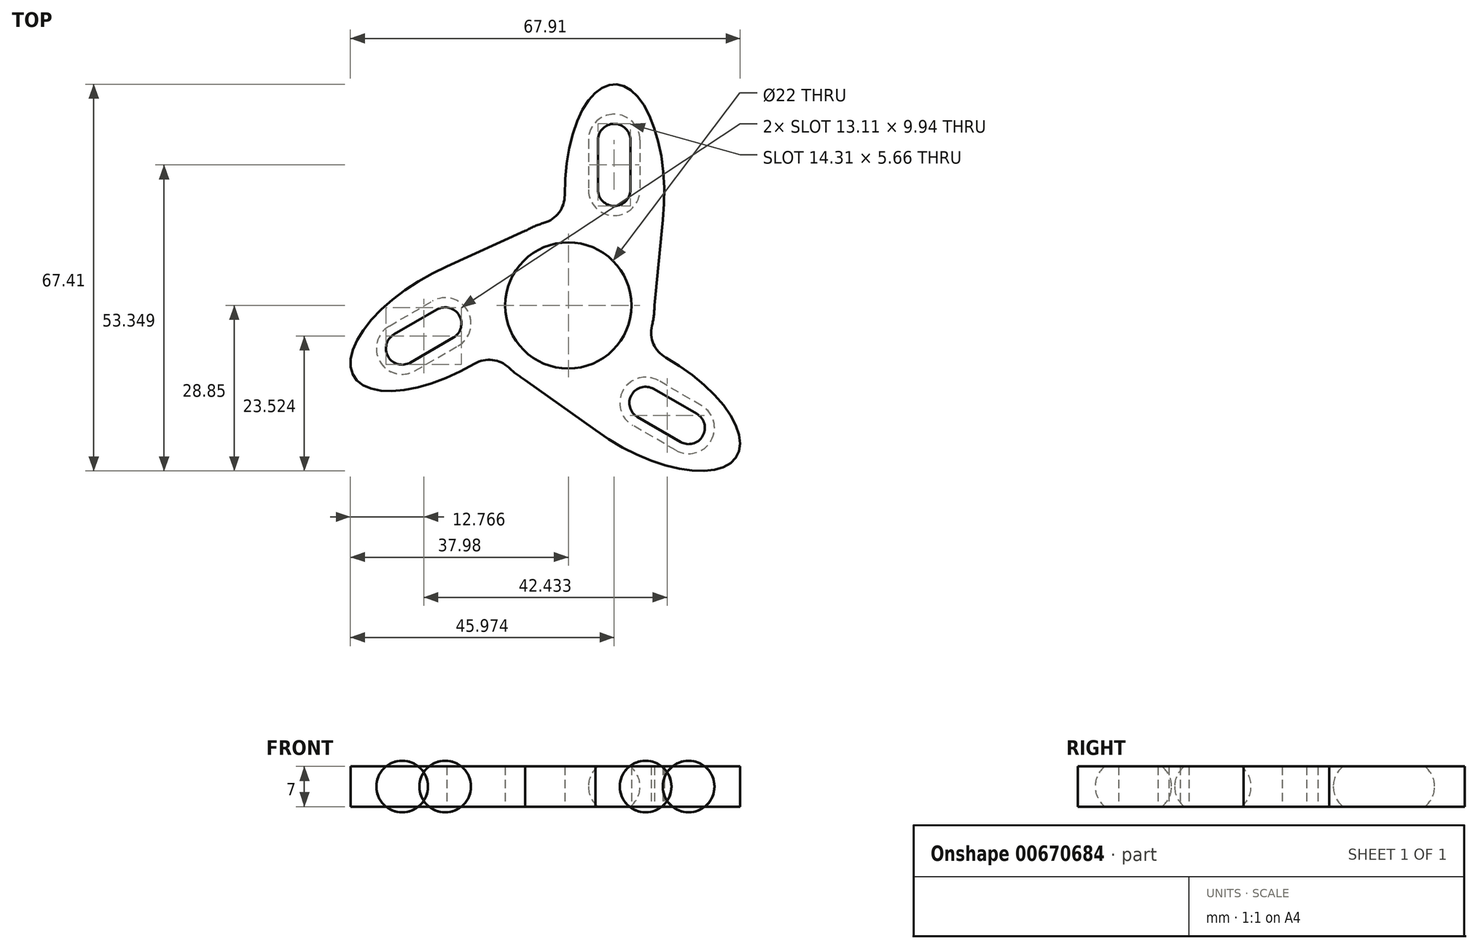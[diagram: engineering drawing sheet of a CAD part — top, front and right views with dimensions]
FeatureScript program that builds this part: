
annotation { "Feature Type Name" : "Feature", "Feature Type Description" : "" }
export const myFeature = defineFeature(function(context is Context, id is Id, definition is map)
    precondition{}
    {
        {
            var Q0;
            Q0=qCreatedBy(makeId("Top.planeOp"),FACE);
            var sketch = newSketch(context, id + "F0", { "sketchPlane" : qUnion([Q0])});
            skCircle(sketch, "E0", {"center": v(0, 0) * mm, "radius": 11 * mm});
            skCircle(sketch, "E1", {"center": v(0, 0) * mm, "radius": 15 * mm});
            skLineSegment(sketch, "E2", {"start": v(3.5, 28.83) * mm, "end": v(3.5, 20.17) * mm});
            skArc(sketch, "E3", {"start": v(3.5, 28.83) * mm, "mid": v(4.81, 32) * mm, "end": v(8, 33.33) * mm});
            skArc(sketch, "E4", {"start": v(3.5, 20.17) * mm, "mid": v(4.81, 16.99) * mm, "end": v(8, 15.67) * mm});
            skLineSegment(sketch, "E5", {"start": v(8, 33.33) * mm, "end": v(8, 15.67) * mm});
            skEllipse(sketch, "E6", {"center": v(8.05, 19.5) * mm, "majorRadius": 19.05 * mm, "minorRadius": 8.67 * mm, "majorAxis": v(0, 1)});
            skLineSegment(sketch, "E7", {"start": v(15, 0) * mm, "end": v(16.47, 14.94) * mm});
            skLineSegment(sketch, "E8.1.0", {"start": v(-32.86, -9.74) * mm, "end": v(-17.57, -0.91) * mm});
            skLineSegment(sketch, "E8.1.1", {"start": v(-26.71, -11.39) * mm, "end": v(-19.21, -7.06) * mm});
            skArc(sketch, "E8.1.2", {"start": v(-19.21, -7.06) * mm, "mid": v(-17.12, -4.33) * mm, "end": v(-17.57, -0.91) * mm});
            skEllipse(sketch, "E8.1.3", {"center": v(-20.92, -2.79) * mm, "majorRadius": 19.05 * mm, "minorRadius": 8.67 * mm, "majorAxis": v(-0.87, -0.5)});
            skLineSegment(sketch, "E8.1.5", {"start": v(-7.5, 13) * mm, "end": v(-21.18, 6.79) * mm});
            skLineSegment(sketch, "E8.2.0", {"start": v(24.87, -23.59) * mm, "end": v(9.57, -14.76) * mm});
            skLineSegment(sketch, "E8.2.1", {"start": v(23.22, -17.44) * mm, "end": v(15.72, -13.11) * mm});
            skArc(sketch, "E8.2.2", {"start": v(15.72, -13.11) * mm, "mid": v(12.3, -12.66) * mm, "end": v(9.57, -14.76) * mm});
            skEllipse(sketch, "E8.2.3", {"center": v(12.87, -16.72) * mm, "majorRadius": 19.05 * mm, "minorRadius": 8.67 * mm, "majorAxis": v(0.87, -0.5)});
            skLineSegment(sketch, "E8.2.5", {"start": v(-7.5, -13) * mm, "end": v(4.7, -21.73) * mm});
            skArc(sketch, "E9.1.0", {"start": v(-26.71, -11.39) * mm, "mid": v(-30.13, -11.84) * mm, "end": v(-32.86, -9.74) * mm});
            skArc(sketch, "E9.2.0", {"start": v(23.22, -17.44) * mm, "mid": v(25.31, -20.17) * mm, "end": v(24.87, -23.59) * mm});
            skSolve(sketch);
        }
        {
            var Q0;
            Q0=makeQuery(id+"F0.imprint","IMPRINT",FACE,{"disambiguationData":[TD([[makeQuery(id+"F0.imprint","IMPRINT",EDGE,{"derivedFrom":sQuery(id+"F0.wireOp",EDGE,"E8.1.0")}),1.0]])]});
            var Q1;
            Q1=makeQuery(id+"F0.imprint","IMPRINT",FACE,{"disambiguationData":[TD([[makeQuery(id+"F0.imprint","IMPRINT",EDGE,{"derivedFrom":sQuery(id+"F0.wireOp",EDGE,"E8.1.0")}),-1.0]])]});
            var Q2;
            {var subQ0=sQuery(id+"F0.wireOp",EDGE,"E8.1.3");var subQ1=sQuery(id+"F0.wireOp",EDGE,"E0");var subQ2=makeQuery(id+"F0.imprint","INTERSECT",VERTEX,{"disambiguationData":[OD(0.0)],"derivedFrom":[subQ1,subQ0]});Q2=makeQuery(id+"F0.imprint","IMPRINT",FACE,{"disambiguationData":[TD([[makeQuery(id+"F0.imprint","IMPRINT",EDGE,{"disambiguationData":[TD([[subQ2,-1.0]])],"derivedFrom":subQ1}),-1.0]])]});}
            var Q3;
            {var subQ0=sQuery(id+"F0.wireOp",EDGE,"E8.1.5");Q3=makeQuery(id+"F0.imprint","IMPRINT",FACE,{"disambiguationData":[TD([[makeQuery(id+"F0.imprint","IMPRINT",EDGE,{"derivedFrom":subQ0}),1.0]])]});}
            var Q4;
            {var subQ5=sQuery(id+"F0.wireOp",EDGE,"E6");var subQ7=sQuery(id+"F0.wireOp",EDGE,"E0");var subQ8=makeQuery(id+"F0.imprint","INTERSECT",VERTEX,{"disambiguationData":[OD(0.0)],"derivedFrom":[subQ7,subQ5]});Q4=makeQuery(id+"F0.imprint","IMPRINT",FACE,{"disambiguationData":[TD([[makeQuery(id+"F0.imprint","IMPRINT",EDGE,{"disambiguationData":[TD([[subQ8,-1.0]])],"derivedFrom":subQ7}),-1.0]])]});}
            var Q5;
            {var subQ0=sQuery(id+"F0.wireOp",EDGE,"q2KN5mIX-ol61-8E7t-r4eS-oeKXbcaP1ytD");Q5=makeQuery(id+"F0.imprint","IMPRINT",FACE,{"disambiguationData":[TD([[makeQuery(id+"F0.imprint","IMPRINT",EDGE,{"derivedFrom":subQ0}),-1.0]])]});}
            var Q6;
            Q6=makeQuery(id+"F0.imprint","IMPRINT",FACE,{"disambiguationData":[TD([[makeQuery(id+"F0.imprint","IMPRINT",EDGE,{"derivedFrom":sQuery(id+"F0.wireOp",EDGE,"E2")}),-1.0]])]});
            var Q7;
            {var subQ0=sQuery(id+"F0.wireOp",EDGE,"E6");var subQ1=sQuery(id+"F0.wireOp",EDGE,"E0");var subQ2=makeQuery(id+"F0.imprint","INTERSECT",VERTEX,{"disambiguationData":[OD(0.0)],"derivedFrom":[subQ1,subQ0]});Q7=makeQuery(id+"F0.imprint","IMPRINT",FACE,{"disambiguationData":[TD([[makeQuery(id+"F0.imprint","IMPRINT",EDGE,{"disambiguationData":[TD([[subQ2,1.0]])],"derivedFrom":subQ1}),-1.0]])]});}
            var Q8;
            Q8=makeQuery(id+"F0.imprint","IMPRINT",FACE,{"disambiguationData":[TD([[makeQuery(id+"F0.imprint","IMPRINT",EDGE,{"derivedFrom":sQuery(id+"F0.wireOp",EDGE,"E2")}),1.0]])]});
            var Q9;
            {var subQ3=sQuery(id+"F0.wireOp",EDGE,"E6");var subQ7=sQuery(id+"F0.wireOp",EDGE,"E0");var subQ8=makeQuery(id+"F0.imprint","INTERSECT",VERTEX,{"disambiguationData":[OD(1.0)],"derivedFrom":[subQ7,subQ3]});Q9=makeQuery(id+"F0.imprint","IMPRINT",FACE,{"disambiguationData":[TD([[makeQuery(id+"F0.imprint","IMPRINT",EDGE,{"disambiguationData":[TD([[subQ8,1.0]])],"derivedFrom":subQ7}),-1.0]])]});}
            var Q10;
            {var subQ0=sQuery(id+"F0.wireOp",EDGE,"E7");Q10=makeQuery(id+"F0.imprint","IMPRINT",FACE,{"disambiguationData":[TD([[makeQuery(id+"F0.imprint","IMPRINT",EDGE,{"derivedFrom":subQ0}),1.0]])]});}
            var Q11;
            {var subQ0=sQuery(id+"F0.wireOp",EDGE,"E8.1.4");Q11=makeQuery(id+"F0.imprint","IMPRINT",FACE,{"disambiguationData":[TD([[makeQuery(id+"F0.imprint","IMPRINT",EDGE,{"derivedFrom":subQ0}),-1.0]])]});}
            var Q12;
            {var subQ4=sQuery(id+"F0.wireOp",EDGE,"E8.1.3");var subQ5=sQuery(id+"F0.wireOp",EDGE,"E0");var subQ6=makeQuery(id+"F0.imprint","INTERSECT",VERTEX,{"disambiguationData":[OD(1.0)],"derivedFrom":[subQ5,subQ4]});Q12=makeQuery(id+"F0.imprint","IMPRINT",FACE,{"disambiguationData":[TD([[makeQuery(id+"F0.imprint","IMPRINT",EDGE,{"disambiguationData":[TD([[subQ6,-1.0]])],"derivedFrom":subQ5}),-1.0]])]});}
            var Q13;
            {var subQ0=sQuery(id+"F0.wireOp",EDGE,"E8.2.5");Q13=makeQuery(id+"F0.imprint","IMPRINT",FACE,{"disambiguationData":[TD([[makeQuery(id+"F0.imprint","IMPRINT",EDGE,{"derivedFrom":subQ0}),1.0]])]});}
            var Q14;
            {var subQ0=sQuery(id+"F0.wireOp",EDGE,"E8.2.3");var subQ1=sQuery(id+"F0.wireOp",EDGE,"E0");var subQ2=makeQuery(id+"F0.imprint","INTERSECT",VERTEX,{"disambiguationData":[OD(0.0)],"derivedFrom":[subQ1,subQ0]});Q14=makeQuery(id+"F0.imprint","IMPRINT",FACE,{"disambiguationData":[TD([[makeQuery(id+"F0.imprint","IMPRINT",EDGE,{"disambiguationData":[TD([[subQ2,-1.0]])],"derivedFrom":subQ1}),-1.0]])]});}
            var Q15;
            Q15=makeQuery(id+"F0.imprint","IMPRINT",FACE,{"disambiguationData":[TD([[makeQuery(id+"F0.imprint","IMPRINT",EDGE,{"derivedFrom":sQuery(id+"F0.wireOp",EDGE,"E8.2.0")}),1.0]])]});
            var Q16;
            Q16=makeQuery(id+"F0.imprint","IMPRINT",FACE,{"disambiguationData":[TD([[makeQuery(id+"F0.imprint","IMPRINT",EDGE,{"derivedFrom":sQuery(id+"F0.wireOp",EDGE,"E8.2.0")}),-1.0]])]});
            var Q17;
            {var subQ0=sQuery(id+"F0.wireOp",EDGE,"E8.2.4");Q17=makeQuery(id+"F0.imprint","IMPRINT",FACE,{"disambiguationData":[TD([[makeQuery(id+"F0.imprint","IMPRINT",EDGE,{"derivedFrom":subQ0}),-1.0]])]});}
            extrude(context, id + "F1", {"entities" : qUnion([Q0, Q1, Q2, Q3, Q4, Q5, Q6, Q7, Q8, Q9, Q10, Q11, Q12, Q13, Q14, Q15, Q16, Q17]), "endBound" : BoundingType.SYMMETRIC, "depth" : 7 * mm, "offsetDistance" : 25 * mm});
        }
        {
            var Q0;
            Q0=makeQuery(id+"F0.imprint","IMPRINT",FACE,{"disambiguationData":[TD([[makeQuery(id+"F0.imprint","IMPRINT",EDGE,{"derivedFrom":sQuery(id+"F0.wireOp",EDGE,"E2")}),1.0]])]});
            var Q1;
            Q1=sQuery(id+"F0.wireOp",EDGE,"E5");
            revolve(context, id + "F2", {"operationType" : NewBodyOperationType.REMOVE, "surfaceOperationType" : NewSurfaceOperationType.NEW, "entities" : qUnion([Q0]), "axis" : qUnion([Q1]), "revolveType" : RevolveType.FULL, "oppositeDirection" : true});
        }
        {
            var Q0;
            Q0=makeQuery(id+"F0.imprint","IMPRINT",FACE,{"disambiguationData":[TD([[makeQuery(id+"F0.imprint","IMPRINT",EDGE,{"derivedFrom":sQuery(id+"F0.wireOp",EDGE,"E8.1.0")}),-1.0]])]});
            var Q1;
            Q1=sQuery(id+"F0.wireOp",EDGE,"E8.1.0");
            revolve(context, id + "F3", {"operationType" : NewBodyOperationType.REMOVE, "surfaceOperationType" : NewSurfaceOperationType.NEW, "entities" : qUnion([Q0]), "axis" : qUnion([Q1]), "revolveType" : RevolveType.FULL, "oppositeDirection" : true});
        }
        {
            var Q0;
            Q0=makeQuery(id+"F0.imprint","IMPRINT",FACE,{"disambiguationData":[TD([[makeQuery(id+"F0.imprint","IMPRINT",EDGE,{"derivedFrom":sQuery(id+"F0.wireOp",EDGE,"E8.2.0")}),-1.0]])]});
            var Q1;
            Q1=sQuery(id+"F0.wireOp",EDGE,"E8.2.0");
            revolve(context, id + "F4", {"operationType" : NewBodyOperationType.REMOVE, "surfaceOperationType" : NewSurfaceOperationType.NEW, "entities" : qUnion([Q0]), "axis" : qUnion([Q1]), "revolveType" : RevolveType.FULL, "oppositeDirection" : true});
        }
        {
            var Q0;
            Q0=makeQuery(id+"F1.opExtrude","SWEPT_EDGE",EDGE,{"disambiguationData":[OSD([sQuery(id+"F0.wireOp",EDGE,"E1"),sQuery(id+"F0.wireOp",EDGE,"E8.2.3")])]});
            var Q1;
            Q1=makeQuery(id+"F1.opExtrude","SWEPT_EDGE",EDGE,{"disambiguationData":[OSD([sQuery(id+"F0.wireOp",EDGE,"E1"),sQuery(id+"F0.wireOp",EDGE,"E8.1.3")])]});
            var Q2;
            Q2=makeQuery(id+"F1.opExtrude","SWEPT_EDGE",EDGE,{"disambiguationData":[OSD([sQuery(id+"F0.wireOp",EDGE,"E1"),sQuery(id+"F0.wireOp",EDGE,"E6")])]});
            fillet(context, id + "F5", {"entities" : qUnion([Q0, Q1, Q2]), "radius" : 5 * mm, "tangentPropagation" : true, "allowEdgeOverflow" : false});
        }
    });
